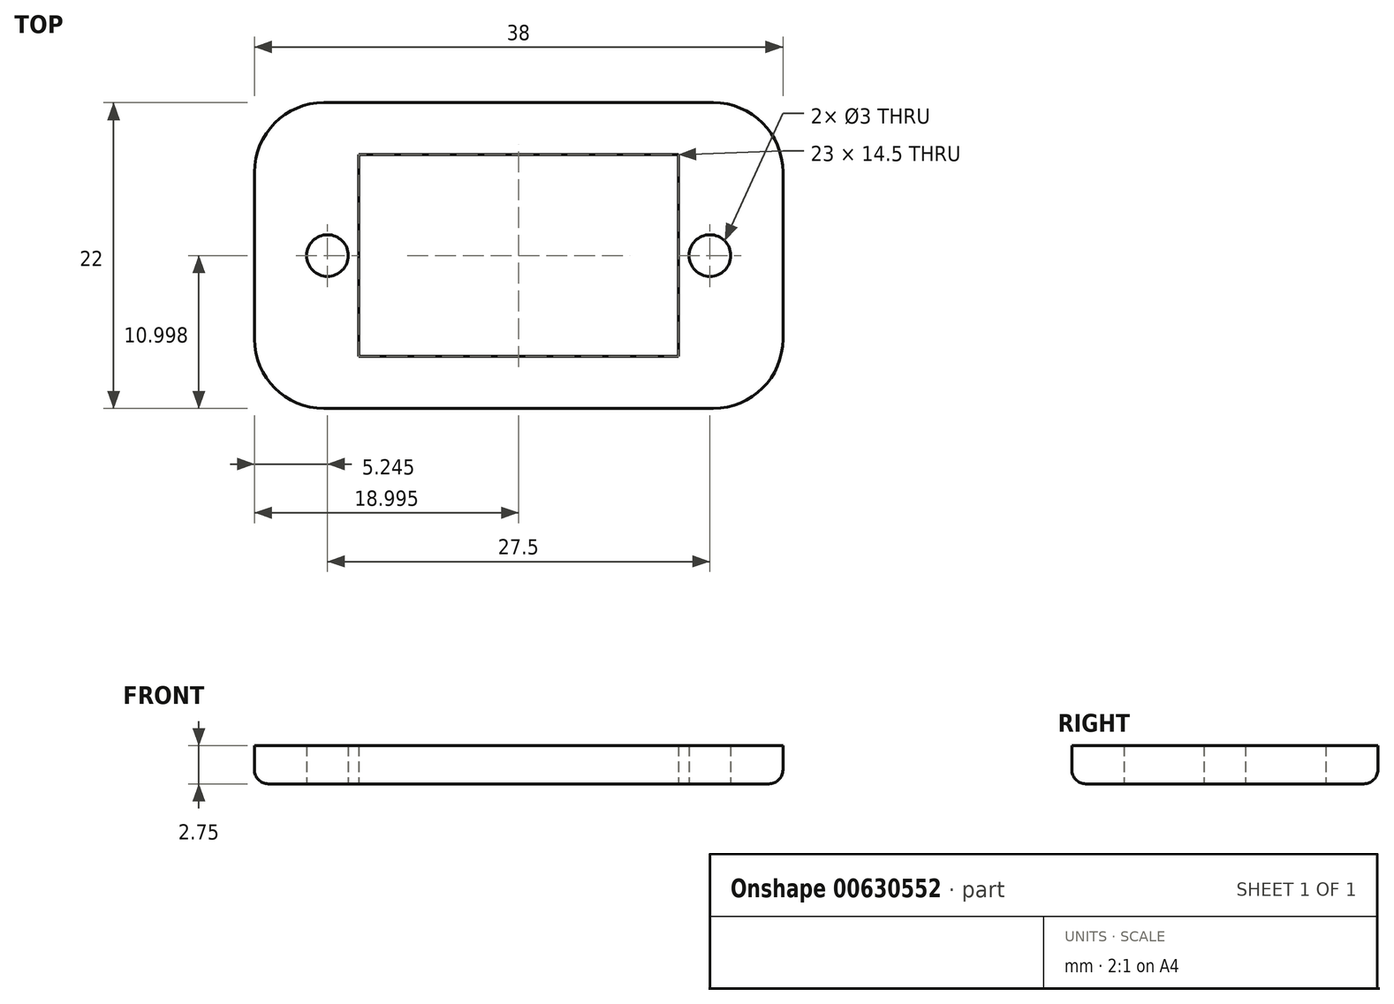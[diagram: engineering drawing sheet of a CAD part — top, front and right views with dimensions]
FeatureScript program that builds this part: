
annotation { "Feature Type Name" : "Feature", "Feature Type Description" : "" }
export const myFeature = defineFeature(function(context is Context, id is Id, definition is map)
    precondition{}
    {
        {
            var Q0;
            Q0=qCreatedBy(makeId("Top.planeOp"),FACE);
            var sketch = newSketch(context, id + "F0", { "sketchPlane" : qUnion([Q0])});
            skLineSegment(sketch, "E0.bottom", {"start": v(-18.86, 9.77) * mm, "end": v(19.14, 9.77) * mm});
            skLineSegment(sketch, "E0.top", {"start": v(-18.86, -12.23) * mm, "end": v(19.14, -12.23) * mm});
            skLineSegment(sketch, "E0.left", {"start": v(-18.86, 9.77) * mm, "end": v(-18.86, -12.23) * mm});
            skLineSegment(sketch, "E0.right", {"start": v(19.14, 9.77) * mm, "end": v(19.14, -12.23) * mm});
            skLineSegment(sketch, "E1.bottom", {"start": v(-11.36, 6.02) * mm, "end": v(11.64, 6.02) * mm});
            skLineSegment(sketch, "E1.top", {"start": v(-11.36, -8.48) * mm, "end": v(11.64, -8.48) * mm});
            skLineSegment(sketch, "E1.left", {"start": v(-11.36, 6.02) * mm, "end": v(-11.36, -8.48) * mm});
            skLineSegment(sketch, "E1.right", {"start": v(11.64, 6.02) * mm, "end": v(11.64, -8.48) * mm});
            skCircle(sketch, "E2", {"center": v(-13.61, -1.23) * mm, "radius": 1.5 * mm});
            skCircle(sketch, "E3", {"center": v(13.89, -1.23) * mm, "radius": 1.5 * mm});
            skSolve(sketch);
        }
        {
            var Q0;
            Q0=makeQuery(id+"F0.imprint","IMPRINT",FACE,{"disambiguationData":[TD([[makeQuery(id+"F0.imprint","IMPRINT",EDGE,{"derivedFrom":sQuery(id+"F0.wireOp",EDGE,"E0.bottom")}),-1.0]])]});
            extrude(context, id + "F1", {"entities" : qUnion([Q0]), "depth" : 2.75 * mm, "offsetDistance" : 25 * mm});
        }
        {
            var Q0;
            Q0=makeQuery(id+"F1.opExtrude","CAP_EDGE",EDGE,{"disambiguationData":[OSD([sQuery(id+"F0.wireOp",EDGE,"E0.right")])],"isStart":true});
            var Q1;
            Q1=makeQuery(id+"F1.opExtrude","CAP_EDGE",EDGE,{"disambiguationData":[OSD([sQuery(id+"F0.wireOp",EDGE,"E0.bottom")])],"isStart":true});
            var Q2;
            Q2=makeQuery(id+"F1.opExtrude","CAP_EDGE",EDGE,{"disambiguationData":[OSD([sQuery(id+"F0.wireOp",EDGE,"E0.left")])],"isStart":true});
            var Q3;
            Q3=makeQuery(id+"F1.opExtrude","CAP_EDGE",EDGE,{"disambiguationData":[OSD([sQuery(id+"F0.wireOp",EDGE,"E0.top")])],"isStart":true});
            fillet(context, id + "F2", {"entities" : qUnion([Q0, Q1, Q2, Q3]), "radius" : 1 * mm, "tangentPropagation" : true, "allowEdgeOverflow" : false});
        }
        {
            var Q0;
            Q0=makeQuery(id+"F1.opExtrude","SWEPT_EDGE",EDGE,{"disambiguationData":[OSD([sQuery(id+"F0.wireOp",EDGE,"E0.bottom"),sQuery(id+"F0.wireOp",EDGE,"E0.right")])]});
            var Q1;
            Q1=makeQuery(id+"F1.opExtrude","SWEPT_EDGE",EDGE,{"disambiguationData":[OSD([sQuery(id+"F0.wireOp",EDGE,"E0.top"),sQuery(id+"F0.wireOp",EDGE,"E0.right")])]});
            var Q2;
            Q2=makeQuery(id+"F1.opExtrude","SWEPT_EDGE",EDGE,{"disambiguationData":[OSD([sQuery(id+"F0.wireOp",EDGE,"E0.top"),sQuery(id+"F0.wireOp",EDGE,"E0.left")])]});
            var Q3;
            Q3=makeQuery(id+"F1.opExtrude","SWEPT_EDGE",EDGE,{"disambiguationData":[OSD([sQuery(id+"F0.wireOp",EDGE,"E0.bottom"),sQuery(id+"F0.wireOp",EDGE,"E0.left")])]});
            fillet(context, id + "F3", {"entities" : qUnion([Q0, Q1, Q2, Q3]), "radius" : 5 * mm, "tangentPropagation" : true, "allowEdgeOverflow" : false});
        }
    });
